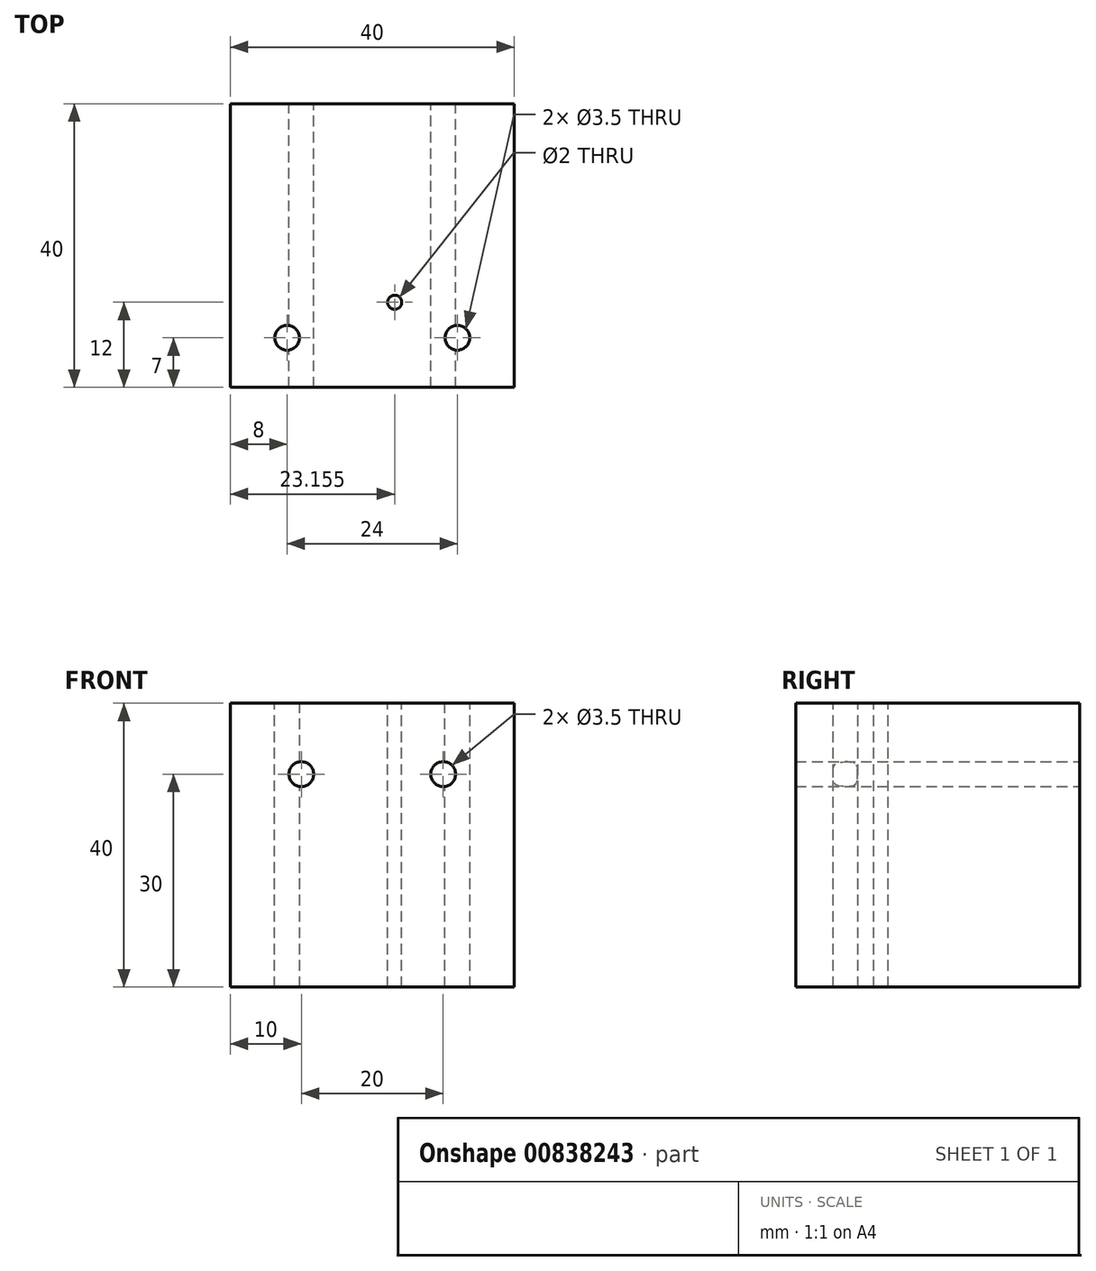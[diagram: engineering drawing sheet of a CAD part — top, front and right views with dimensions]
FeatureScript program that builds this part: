
annotation { "Feature Type Name" : "Feature", "Feature Type Description" : "" }
export const myFeature = defineFeature(function(context is Context, id is Id, definition is map)
    precondition{}
    {
        {
            var Q0;
            Q0=qCreatedBy(makeId("Top.planeOp"),FACE);
            var sketch = newSketch(context, id + "F0", { "sketchPlane" : qUnion([Q0])});
            skLineSegment(sketch, "E0.bottom", {"start": v(-20, 20) * mm, "end": v(20, 20) * mm});
            skLineSegment(sketch, "E0.top", {"start": v(-20, -20) * mm, "end": v(20, -20) * mm});
            skLineSegment(sketch, "E0.left", {"start": v(-20, 20) * mm, "end": v(-20, -20) * mm});
            skLineSegment(sketch, "E0.right", {"start": v(20, 20) * mm, "end": v(20, -20) * mm});
            skPoint(sketch, "E0.middle", {"position": v(0, 0) * mm});
            skLineSegment(sketch, "E1", {"start": v(-20, -13) * mm, "end": v(20, -13) * mm});
            skCircle(sketch, "E2", {"center": v(-12, -13) * mm, "radius": 1.75 * mm});
            skCircle(sketch, "E3", {"center": v(12, -13) * mm, "radius": 1.75 * mm});
            skLineSegment(sketch, "E4", {"start": v(-20, -8) * mm, "end": v(20, -8) * mm});
            skCircle(sketch, "E5", {"center": v(3.16, -8) * mm, "radius": 1 * mm});
            skSolve(sketch);
        }
        {
            var Q0;
            Q0=qCreatedBy(makeId("Front.planeOp"),FACE);
            var sketch = newSketch(context, id + "F1", { "sketchPlane" : qUnion([Q0])});
            skLineSegment(sketch, "E6.bottom", {"start": v(-20, 20) * mm, "end": v(20, 20) * mm});
            skLineSegment(sketch, "E6.top", {"start": v(-20, -20) * mm, "end": v(20, -20) * mm});
            skLineSegment(sketch, "E6.left", {"start": v(-20, 20) * mm, "end": v(-20, -20) * mm});
            skLineSegment(sketch, "E6.right", {"start": v(20, 20) * mm, "end": v(20, -20) * mm});
            skPoint(sketch, "E6.middle", {"position": v(0, 0) * mm});
            skLineSegment(sketch, "E7", {"start": v(-20, 10) * mm, "end": v(20, 10) * mm});
            skCircle(sketch, "E8", {"center": v(-10, 10) * mm, "radius": 1.75 * mm});
            skCircle(sketch, "E9", {"center": v(10, 10) * mm, "radius": 1.75 * mm});
            skSolve(sketch);
        }
        {
            var Q0;
            {var subQ1=sQuery(id+"F1.wireOp",EDGE,"E6.top");Q0=makeQuery(id+"F1.imprint","IMPRINT",FACE,{"disambiguationData":[TD([[makeQuery(id+"F1.imprint","IMPRINT",EDGE,{"derivedFrom":subQ1}),1.0]])]});}
            var Q1;
            {var subQ6=sQuery(id+"F1.wireOp",EDGE,"E6.bottom");Q1=makeQuery(id+"F1.imprint","IMPRINT",FACE,{"disambiguationData":[TD([[makeQuery(id+"F1.imprint","IMPRINT",EDGE,{"derivedFrom":subQ6}),-1.0]])]});}
            extrude(context, id + "F2", {"entities" : qUnion([Q0, Q1]), "depth" : 40 * mm, "offsetDistance" : 25 * mm, "symmetric" : true});
        }
        {
            var Q0;
            {var subQ0=sQuery(id+"F0.wireOp",EDGE,"E2");var subQ1=sQuery(id+"F0.wireOp",EDGE,"E1");var subQ2=makeQuery(id+"F0.imprint","INTERSECT",VERTEX,{"disambiguationData":[OD(0.0)],"derivedFrom":[subQ1,subQ0]});Q0=makeQuery(id+"F0.imprint","IMPRINT",FACE,{"disambiguationData":[TD([[makeQuery(id+"F0.imprint","IMPRINT",EDGE,{"disambiguationData":[TD([[subQ2,-1.0]])],"derivedFrom":subQ1}),1.0]])]});}
            var Q1;
            {var subQ0=sQuery(id+"F0.wireOp",EDGE,"E2");var subQ1=sQuery(id+"F0.wireOp",EDGE,"E1");var subQ2=makeQuery(id+"F0.imprint","INTERSECT",VERTEX,{"disambiguationData":[OD(0.0)],"derivedFrom":[subQ1,subQ0]});Q1=makeQuery(id+"F0.imprint","IMPRINT",FACE,{"disambiguationData":[TD([[makeQuery(id+"F0.imprint","IMPRINT",EDGE,{"disambiguationData":[TD([[subQ2,-1.0]])],"derivedFrom":subQ1}),-1.0]])]});}
            var Q2;
            {var subQ0=sQuery(id+"F0.wireOp",EDGE,"E3");var subQ1=sQuery(id+"F0.wireOp",EDGE,"E1");var subQ2=makeQuery(id+"F0.imprint","INTERSECT",VERTEX,{"disambiguationData":[OD(0.0)],"derivedFrom":[subQ1,subQ0]});Q2=makeQuery(id+"F0.imprint","IMPRINT",FACE,{"disambiguationData":[TD([[makeQuery(id+"F0.imprint","IMPRINT",EDGE,{"disambiguationData":[TD([[subQ2,-1.0]])],"derivedFrom":subQ1}),1.0]])]});}
            var Q3;
            {var subQ0=sQuery(id+"F0.wireOp",EDGE,"E3");var subQ1=sQuery(id+"F0.wireOp",EDGE,"E1");var subQ2=makeQuery(id+"F0.imprint","INTERSECT",VERTEX,{"disambiguationData":[OD(0.0)],"derivedFrom":[subQ1,subQ0]});Q3=makeQuery(id+"F0.imprint","IMPRINT",FACE,{"disambiguationData":[TD([[makeQuery(id+"F0.imprint","IMPRINT",EDGE,{"disambiguationData":[TD([[subQ2,-1.0]])],"derivedFrom":subQ1}),-1.0]])]});}
            var Q4;
            {var subQ0=sQuery(id+"F0.wireOp",EDGE,"E5");var subQ1=sQuery(id+"F0.wireOp",EDGE,"E4");var subQ2=makeQuery(id+"F0.imprint","INTERSECT",VERTEX,{"disambiguationData":[OD(0.0)],"derivedFrom":[subQ1,subQ0]});Q4=makeQuery(id+"F0.imprint","IMPRINT",FACE,{"disambiguationData":[TD([[makeQuery(id+"F0.imprint","IMPRINT",EDGE,{"disambiguationData":[TD([[subQ2,-1.0]])],"derivedFrom":subQ1}),1.0]])]});}
            var Q5;
            {var subQ0=sQuery(id+"F0.wireOp",EDGE,"E5");var subQ1=sQuery(id+"F0.wireOp",EDGE,"E4");var subQ2=makeQuery(id+"F0.imprint","INTERSECT",VERTEX,{"disambiguationData":[OD(0.0)],"derivedFrom":[subQ1,subQ0]});Q5=makeQuery(id+"F0.imprint","IMPRINT",FACE,{"disambiguationData":[TD([[makeQuery(id+"F0.imprint","IMPRINT",EDGE,{"disambiguationData":[TD([[subQ2,-1.0]])],"derivedFrom":subQ1}),-1.0]])]});}
            extrude(context, id + "F3", {"entities" : qUnion([Q0, Q1, Q2, Q3, Q4, Q5]), "operationType" : NewBodyOperationType.REMOVE, "oppositeDirection" : true, "depth" : 40 * mm, "offsetDistance" : 25 * mm, "symmetric" : true});
        }
    });
